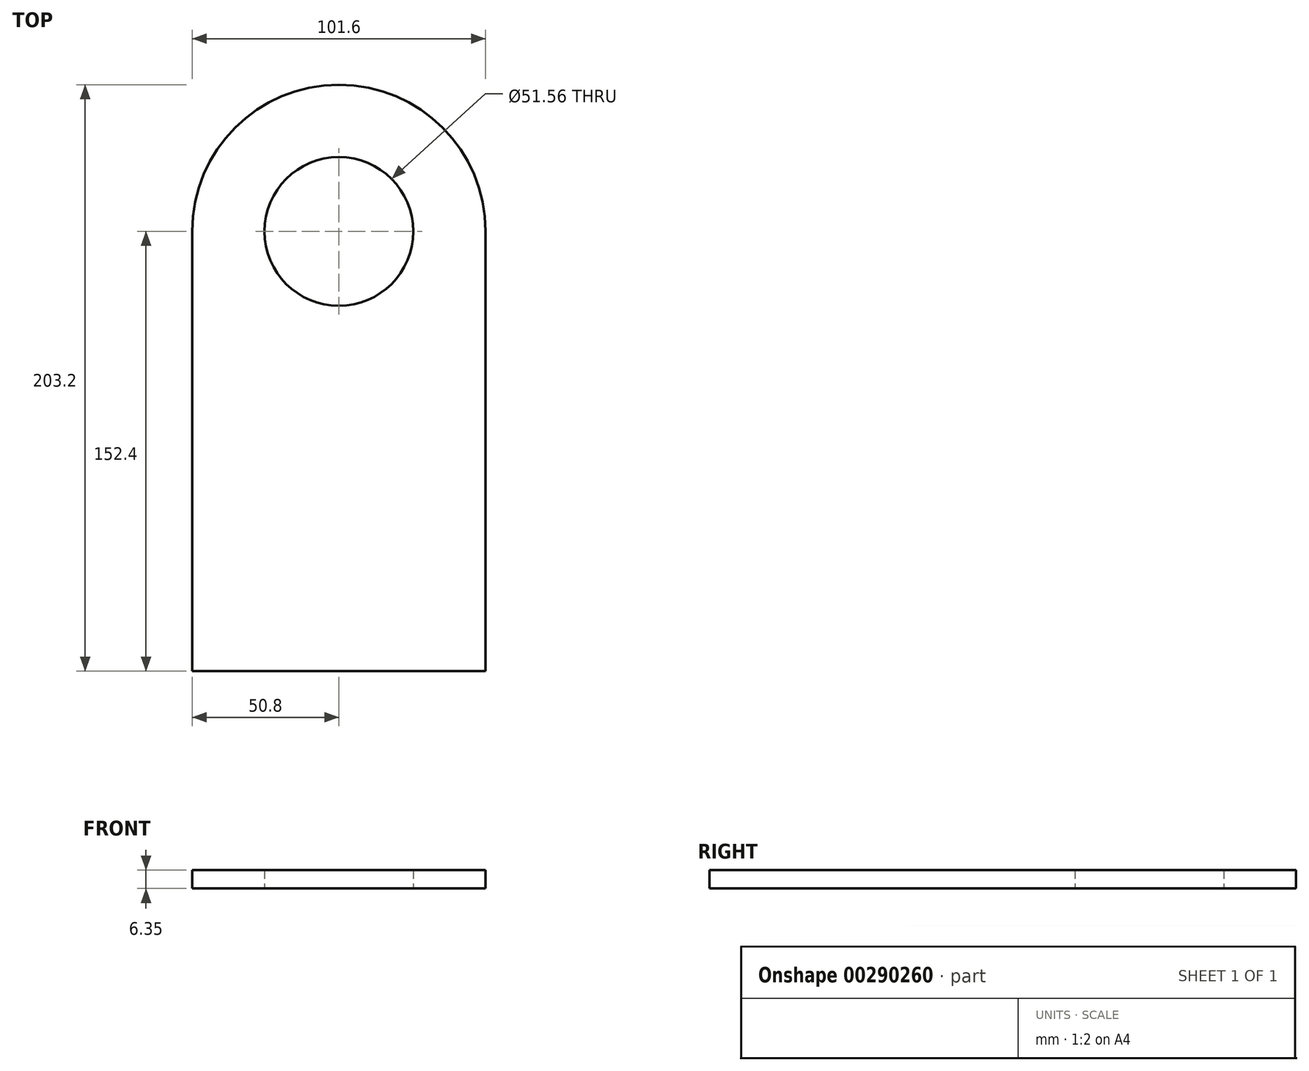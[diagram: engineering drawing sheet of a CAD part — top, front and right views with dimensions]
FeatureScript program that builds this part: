
annotation { "Feature Type Name" : "Feature", "Feature Type Description" : "" }
export const myFeature = defineFeature(function(context is Context, id is Id, definition is map)
    precondition{}
    {
        {
            var Q0;
            Q0=qCreatedBy(makeId("Top.planeOp"),FACE);
            var sketch = newSketch(context, id + "F0", { "sketchPlane" : qUnion([Q0])});
            skLineSegment(sketch, "E0.bottom", {"start": v(0, 0) * mm, "end": v(101.6, 0) * mm});
            skLineSegment(sketch, "E0.left", {"start": v(0, 0) * mm, "end": v(0, 152.4) * mm});
            skLineSegment(sketch, "E0.right", {"start": v(101.6, 0) * mm, "end": v(101.6, 152.4) * mm});
            skCircle(sketch, "E1", {"center": v(50.8, 152.4) * mm, "radius": 25.78 * mm});
            skArc(sketch, "E2", {"start": v(101.6, 152.4) * mm, "mid": v(50.8, 203.2) * mm, "end": v(0, 152.4) * mm});
            skSolve(sketch);
        }
        {
            var Q0;
            Q0 = qSketchRegion(id + "F0", true);
            extrude(context, id + "F1", {"entities" : qUnion([Q0]), "depth" : 6.35 * mm});
        }
    });
